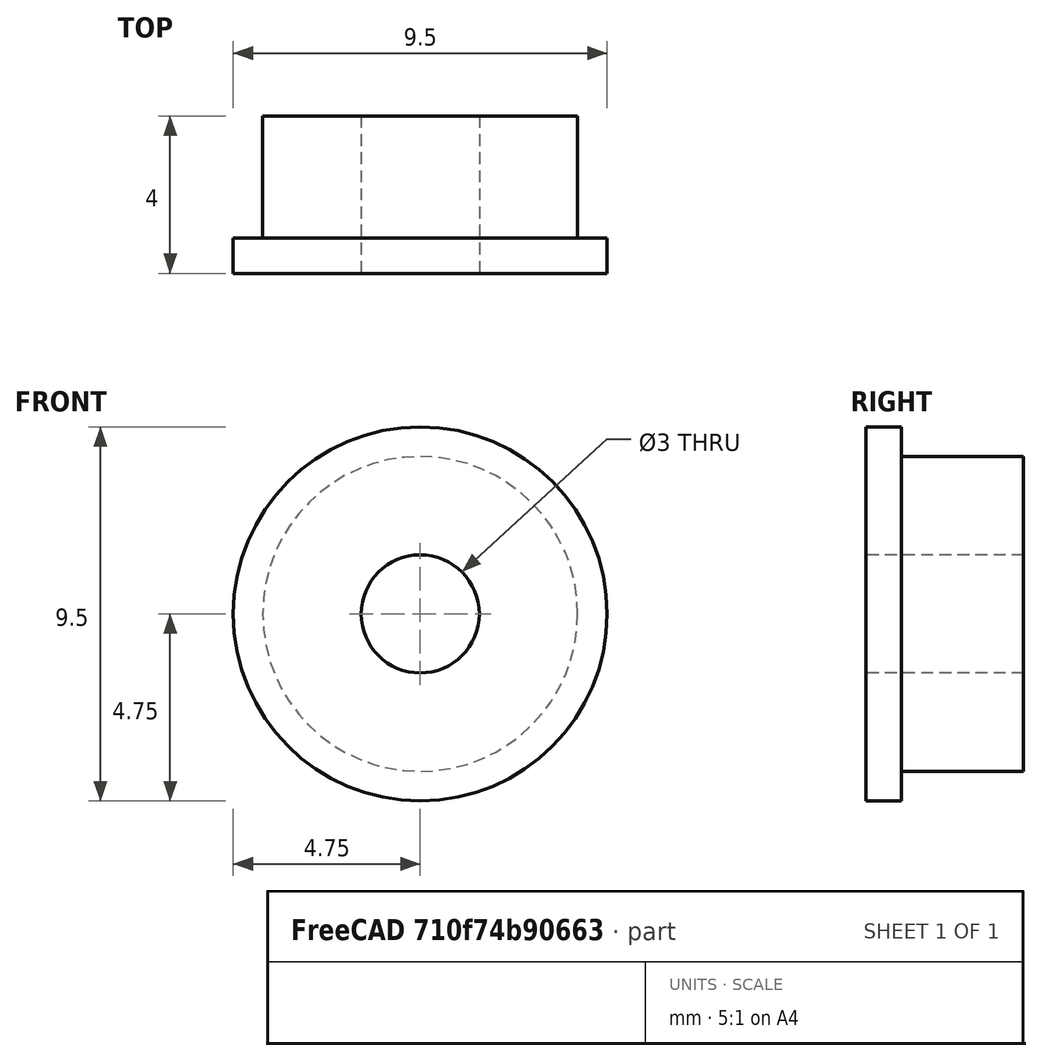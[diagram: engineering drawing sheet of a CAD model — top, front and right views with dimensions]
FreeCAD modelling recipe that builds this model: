
FCSTD DOCUMENT  (FreeCAD 0.16R6706 (Git))
Label: F693ZZ_ball_bearing
License: CreativeCommons Attribution-ShareAlike
LicenseURL: http://creativecommons.org/licenses/by-sa/4.0/
objects: Sketcher::SketchObject×1, PartDesign::Revolution×1
note: 3 computed .brp shape members not serialized (recipe doc carries the construction recipe); baked Part::Feature solids carry a one-line shape summary decoded from their .brp

FEATURE [Sketcher::SketchObject] Sketch  label="Sketch-main"
  sketch-geometry (6):
    g0: LineSegment StartX=1.5 StartY=0 StartZ=0 EndX=4.75 EndY=0 EndZ=0
    g1: LineSegment StartX=4.75 StartY=0 StartZ=0 EndX=4.75 EndY=0.9 EndZ=0
    g2: LineSegment StartX=4.75 StartY=0.9 StartZ=0 EndX=4 EndY=0.9 EndZ=0
    g3: LineSegment StartX=4 StartY=0.9 StartZ=0 EndX=4 EndY=4 EndZ=0
    g4: LineSegment StartX=4 StartY=4 StartZ=0 EndX=1.5 EndY=4 EndZ=0
    g5: LineSegment StartX=1.5 StartY=4 StartZ=0 EndX=1.5 EndY=0 EndZ=0
  constraints (18):
    c: PointOnObject(g0,g-1)
    c: PointOnObject(g0,g-1)
    c: Coincident(g0,g1)
    c: Coincident(g1,g2)
    c: Horizontal(g2)
    c: Coincident(g2,g3)
    c: Coincident(g3,g4)
    c: Coincident(g4,g5)
    c: Coincident(g5,g0)
    c: Vertical(g5)
    c: Horizontal(g4)
    c: Vertical(g3)
    c: Vertical(g1)
    c: DistanceX(g-1,g3) = 4
    c: DistanceX(g-1,g4) = 1.5
    c: DistanceX(g-1,g0) = 4.75
    c: DistanceY(g0,g3) = 4
    c: DistanceY(g1,g3) = 3.1
FEATURE [PartDesign::Revolution] Revolution
  Angle = 360
  Axis = (0,1,0)
  Base = (0,0,0)
  ReferenceAxis = -> Sketch [V_Axis]
  Reversed = true
  Sketch = -> Sketch
